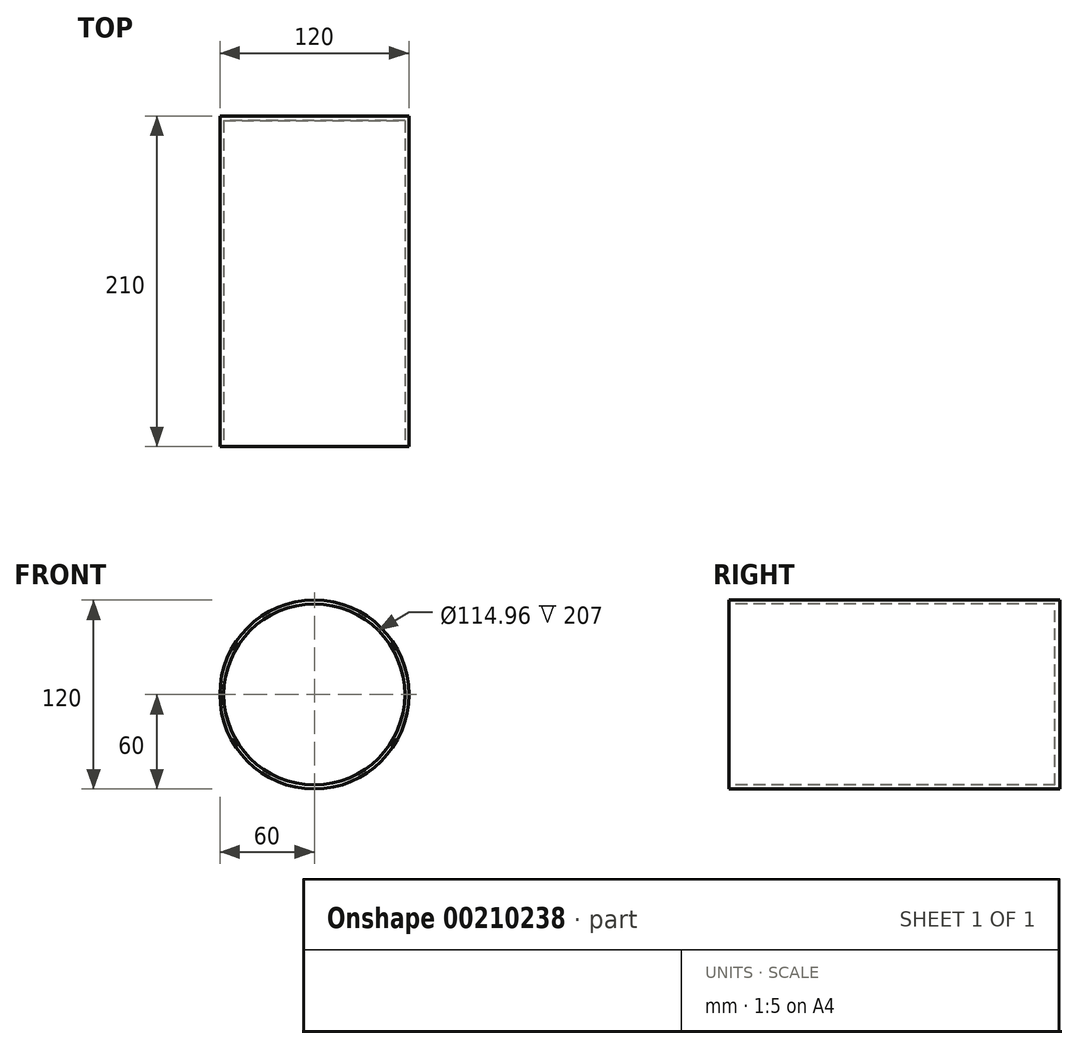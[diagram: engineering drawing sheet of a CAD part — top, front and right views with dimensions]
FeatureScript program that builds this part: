
annotation { "Feature Type Name" : "Feature", "Feature Type Description" : "" }
export const myFeature = defineFeature(function(context is Context, id is Id, definition is map)
    precondition{}
    {
        {
            var Q0;
            Q0=qCreatedBy(makeId("Front.planeOp"),FACE);
            var sketch = newSketch(context, id + "F0", { "sketchPlane" : qUnion([Q0])});
            skCircle(sketch, "E0", {"center": v(0, 0) * mm, "radius": 60 * mm});
            skSolve(sketch);
        }
        {
            var Q0;
            Q0 = qSketchRegion(id + "F0", true);
            extrude(context, id + "F1", {"entities" : qUnion([Q0]), "endBound" : BoundingType.SYMMETRIC, "depth" : 210 * mm});
        }
        {
            var Q0;
            Q0=makeQuery(id+"F1.opExtrude","CAP_FACE",FACE,{"disambiguationData":[OSD([sQuery(id+"F0.wireOp",EDGE,"E0")])],"isStart":false});
            var sketch = newSketch(context, id + "F2", { "sketchPlane" : qUnion([Q0])});
            skCircle(sketch, "E1", {"center": v(0, 0) * mm, "radius": 57.48 * mm});
            skSolve(sketch);
        }
        {
            var Q0;
            Q0 = qSketchRegion(id + "F2", true);
            extrude(context, id + "F3", {"entities" : qUnion([Q0]), "operationType" : NewBodyOperationType.REMOVE, "oppositeDirection" : true, "depth" : 207 * mm});
        }
    });
